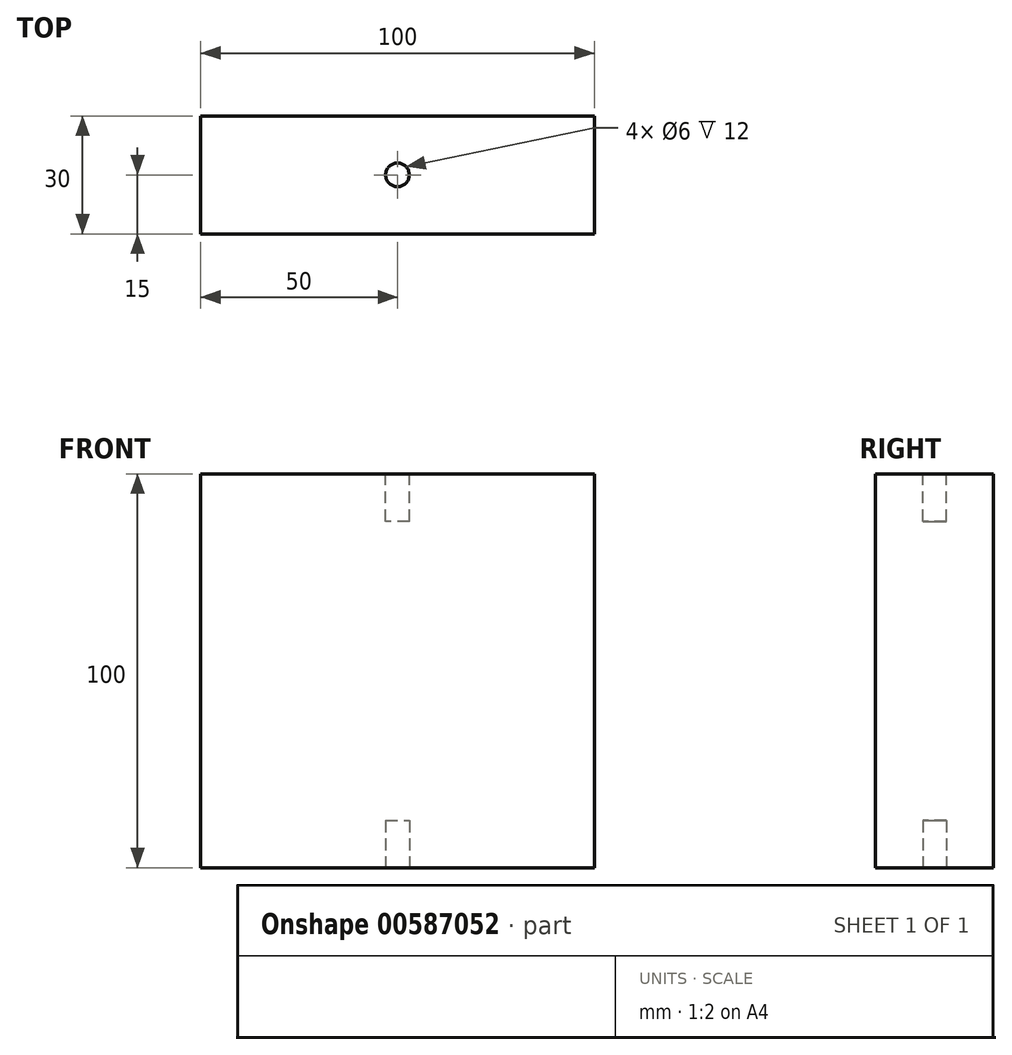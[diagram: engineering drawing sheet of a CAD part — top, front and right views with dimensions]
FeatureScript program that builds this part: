
annotation { "Feature Type Name" : "Feature", "Feature Type Description" : "" }
export const myFeature = defineFeature(function(context is Context, id is Id, definition is map)
    precondition{}
    {
        {
            var Q0;
            Q0=qCreatedBy(makeId("Top.planeOp"),FACE);
            var sketch = newSketch(context, id + "F0", { "sketchPlane" : qUnion([Q0])});
            skLineSegment(sketch, "E0.bottom", {"start": v(0, 0) * mm, "end": v(100, 0) * mm});
            skLineSegment(sketch, "E0.top", {"start": v(0, 30) * mm, "end": v(100, 30) * mm});
            skLineSegment(sketch, "E0.left", {"start": v(0, 0) * mm, "end": v(0, 30) * mm});
            skLineSegment(sketch, "E0.right", {"start": v(100, 0) * mm, "end": v(100, 30) * mm});
            skSolve(sketch);
        }
        {
            var Q0;
            Q0=makeQuery(id+"F0.imprint","IMPRINT",FACE,{"disambiguationData":[TD([[makeQuery(id+"F0.imprint","IMPRINT",EDGE,{"derivedFrom":sQuery(id+"F0.wireOp",EDGE,"E0.bottom")}),1.0]])]});
            extrude(context, id + "F1", {"entities" : qUnion([Q0]), "depth" : 100 * mm, "offsetDistance" : 25 * mm});
        }
        {
            var Q0;
            Q0=makeQuery(id+"F1.opExtrude","CAP_FACE",FACE,{"disambiguationData":[OSD([sQuery(id+"F0.wireOp",EDGE,"E0.bottom"),sQuery(id+"F0.wireOp",EDGE,"E0.top"),sQuery(id+"F0.wireOp",EDGE,"E0.left"),sQuery(id+"F0.wireOp",EDGE,"E0.right")])],"isStart":true});
            var sketch = newSketch(context, id + "F2", { "sketchPlane" : qUnion([Q0])});
            skCircle(sketch, "E1", {"center": v(50, -15) * mm, "radius": 3 * mm});
            skPoint(sketch, "E1.centerSnap0", {"position": v(50, -30) * mm});
            skPoint(sketch, "E1.centerSnap1", {"position": v(100, -15) * mm});
            skSolve(sketch);
        }
        {
            var Q0;
            Q0=makeQuery(id+"F2.imprint","IMPRINT",FACE,{"disambiguationData":[TD([[makeQuery(id+"F2.imprint","IMPRINT",EDGE,{"derivedFrom":sQuery(id+"F2.wireOp",EDGE,"E1")}),1.0]])]});
            extrude(context, id + "F3", {"entities" : qUnion([Q0]), "operationType" : NewBodyOperationType.REMOVE, "oppositeDirection" : true, "depth" : 12 * mm, "offsetDistance" : 25 * mm});
        }
        {
            var Q0;
            Q0=makeQuery(id+"F1.opExtrude","CAP_FACE",FACE,{"disambiguationData":[OSD([sQuery(id+"F0.wireOp",EDGE,"E0.bottom"),sQuery(id+"F0.wireOp",EDGE,"E0.top"),sQuery(id+"F0.wireOp",EDGE,"E0.left"),sQuery(id+"F0.wireOp",EDGE,"E0.right")])],"isStart":false});
            var sketch = newSketch(context, id + "F4", { "sketchPlane" : qUnion([Q0])});
            skCircle(sketch, "E2", {"center": v(50, 15) * mm, "radius": 3 * mm});
            skPoint(sketch, "E2.centerSnap0", {"position": v(50, 30) * mm});
            skPoint(sketch, "E2.centerSnap1", {"position": v(100, 15) * mm});
            skSolve(sketch);
        }
        {
            var Q0;
            Q0=makeQuery(id+"F4.imprint","IMPRINT",FACE,{"disambiguationData":[TD([[makeQuery(id+"F4.imprint","IMPRINT",EDGE,{"derivedFrom":sQuery(id+"F4.wireOp",EDGE,"E2")}),1.0]])]});
            extrude(context, id + "F5", {"entities" : qUnion([Q0]), "operationType" : NewBodyOperationType.REMOVE, "oppositeDirection" : true, "depth" : 12 * mm, "offsetDistance" : 25 * mm});
        }
    });
